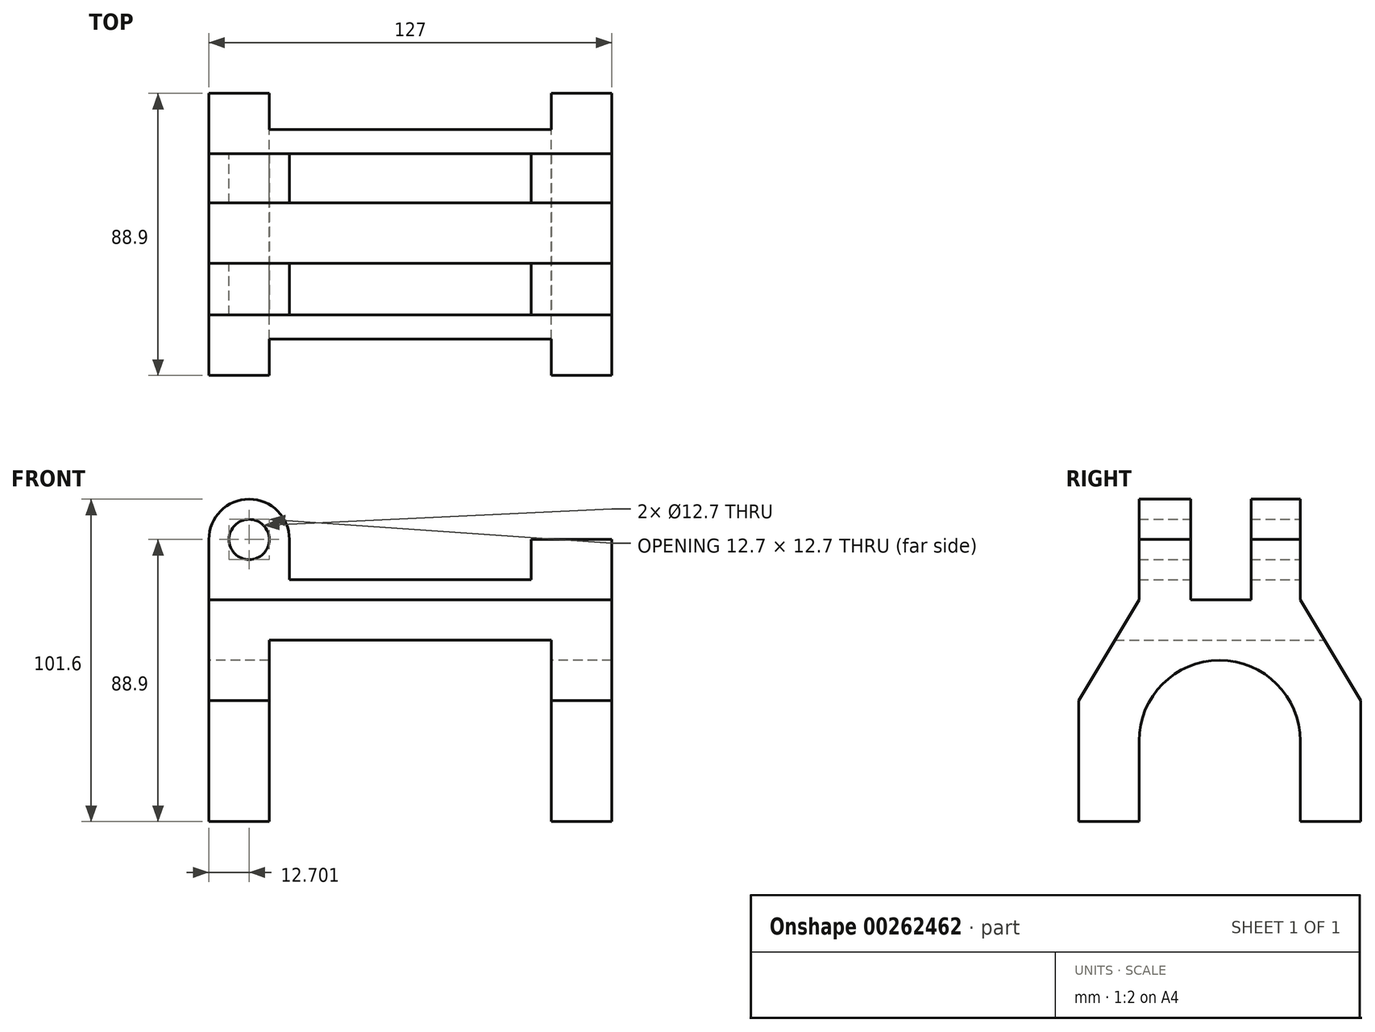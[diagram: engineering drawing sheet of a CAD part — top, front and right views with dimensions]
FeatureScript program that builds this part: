
annotation { "Feature Type Name" : "Feature", "Feature Type Description" : "" }
export const myFeature = defineFeature(function(context is Context, id is Id, definition is map)
    precondition{}
    {
        {
            var Q0;
            Q0=qCreatedBy(makeId("Front.planeOp"),FACE);
            var sketch = newSketch(context, id + "F0", { "sketchPlane" : qUnion([Q0])});
            skLineSegment(sketch, "E0.top", {"start": v(-38.24, -43.04) * mm, "end": v(-19.19, -43.04) * mm});
            skLineSegment(sketch, "E0.left", {"start": v(-38.24, 14.1) * mm, "end": v(-38.24, -43.04) * mm});
            skLineSegment(sketch, "E0.right", {"start": v(-19.19, 14.1) * mm, "end": v(-19.19, -43.04) * mm});
            skLineSegment(sketch, "E1.bottom", {"start": v(-19.19, 14.1) * mm, "end": v(69.71, 14.1) * mm});
            skLineSegment(sketch, "E1.top", {"start": v(-12.84, 33.16) * mm, "end": v(63.36, 33.16) * mm});
            skLineSegment(sketch, "E1.left", {"start": v(-38.24, 14.1) * mm, "end": v(-38.24, 33.16) * mm});
            skLineSegment(sketch, "E1.right", {"start": v(88.76, 14.1) * mm, "end": v(88.76, 33.16) * mm});
            skLineSegment(sketch, "E2.top", {"start": v(88.76, -43.04) * mm, "end": v(69.71, -43.04) * mm});
            skLineSegment(sketch, "E2.left", {"start": v(88.76, 14.1) * mm, "end": v(88.76, -43.04) * mm});
            skLineSegment(sketch, "E2.right", {"start": v(69.71, 14.1) * mm, "end": v(69.71, -43.04) * mm});
            skLineSegment(sketch, "E3.top", {"start": v(88.76, 45.86) * mm, "end": v(63.36, 45.86) * mm});
            skLineSegment(sketch, "E3.left", {"start": v(88.76, 33.16) * mm, "end": v(88.76, 45.86) * mm});
            skLineSegment(sketch, "E3.right", {"start": v(63.36, 33.16) * mm, "end": v(63.36, 45.86) * mm});
            skArc(sketch, "E4", {"start": v(-12.84, 45.86) * mm, "mid": v(-25.54, 58.56) * mm, "end": v(-38.24, 45.86) * mm});
            skCircle(sketch, "E5", {"center": v(-25.54, 45.86) * mm, "radius": 6.35 * mm});
            skLineSegment(sketch, "E6", {"start": v(-38.24, 45.86) * mm, "end": v(-38.24, 33.16) * mm});
            skLineSegment(sketch, "E7", {"start": v(-12.84, 45.86) * mm, "end": v(-12.84, 33.16) * mm});
            skSolve(sketch);
        }
        {
            var Q0;
            Q0=qSketchRegion(id+"F0",true);
            extrude(context, id + "F1", {"entities" : qUnion([Q0]), "depth" : 88.9 * mm});
        }
        {
            var Q0;
            Q0=makeQuery(id+"F1.opExtrude","SWEPT_FACE",FACE,{"disambiguationData":[OSD([sQuery(id+"F0.wireOp",EDGE,"E0.left"),sQuery(id+"F0.wireOp",EDGE,"E1.left"),sQuery(id+"F0.wireOp",EDGE,"E6")])]});
            var sketch = newSketch(context, id + "F2", { "sketchPlane" : qUnion([Q0])});
            skPoint(sketch, "E8.centerSnap0", {"position": v(44.45, -43.04) * mm});
            skLineSegment(sketch, "E9", {"start": v(19.05, -17.64) * mm, "end": v(19.05, -43.04) * mm});
            skLineSegment(sketch, "E10", {"start": v(69.85, -17.64) * mm, "end": v(69.85, -43.04) * mm});
            skArc(sketch, "E11", {"start": v(69.85, -17.64) * mm, "mid": v(44.45, 7.76) * mm, "end": v(19.05, -17.64) * mm});
            skLineSegment(sketch, "E12", {"start": v(88.9, -4.94) * mm, "end": v(69.85, 26.8) * mm});
            skLineSegment(sketch, "E13", {"start": v(0, -4.94) * mm, "end": v(19.05, 26.8) * mm});
            skLineSegment(sketch, "E14", {"start": v(19.05, 26.8) * mm, "end": v(19.05, 58.56) * mm});
            skLineSegment(sketch, "E15", {"start": v(69.85, 58.56) * mm, "end": v(69.85, 26.8) * mm});
            skLineSegment(sketch, "E16", {"start": v(44.45, 26.8) * mm, "end": v(53.58, 26.8) * mm});
            skLineSegment(sketch, "E17", {"start": v(34.53, 26.8) * mm, "end": v(44.45, 26.8) * mm});
            skLineSegment(sketch, "E18", {"start": v(34.53, 58.56) * mm, "end": v(34.53, 26.8) * mm});
            skLineSegment(sketch, "E19", {"start": v(53.58, 26.8) * mm, "end": v(53.58, 58.56) * mm});
            skPoint(sketch, "E20.start.orphan", {"position": v(44.45, 61.13) * mm});
            skPoint(sketch, "E21.orphan", {"position": v(19.05, 61.13) * mm});
            skPoint(sketch, "E22.orphan", {"position": v(53.58, 61.13) * mm});
            skPoint(sketch, "E23.orphan", {"position": v(69.85, 61.13) * mm});
            skPoint(sketch, "E24.start.orphan", {"position": v(88.9, 45.86) * mm});
            skPoint(sketch, "E25.orphan", {"position": v(88.9, 58.56) * mm});
            skLineSegment(sketch, "E26", {"start": v(19.05, 58.56) * mm, "end": v(0, 58.56) * mm});
            skLineSegment(sketch, "E27", {"start": v(0, 58.56) * mm, "end": v(0, -4.94) * mm});
            skLineSegment(sketch, "E28", {"start": v(69.85, 58.56) * mm, "end": v(88.9, 58.56) * mm});
            skLineSegment(sketch, "E29", {"start": v(88.9, -4.94) * mm, "end": v(88.9, 58.56) * mm});
            skLineSegment(sketch, "E30", {"start": v(34.53, 58.56) * mm, "end": v(53.58, 58.56) * mm});
            skSolve(sketch);
        }
        {
            var Q0;
            Q0=qSketchRegion(id+"F2",true);
            var Q1;
            {var subQ0=sQuery(id+"F2.wireOp",EDGE,"E9");Q1=makeQuery(id+"F2.imprint","IMPRINT",FACE,{"disambiguationData":[TD([[makeQuery(id+"F2.imprint","IMPRINT",EDGE,{"derivedFrom":subQ0}),1.0]])]});}
            extrude(context, id + "F3", {"entities" : qUnion([Q0, Q1]), "operationType" : NewBodyOperationType.REMOVE, "endBound" : BoundingType.THROUGH_ALL, "oppositeDirection" : true, "depth" : 127 * mm});
        }
    });
